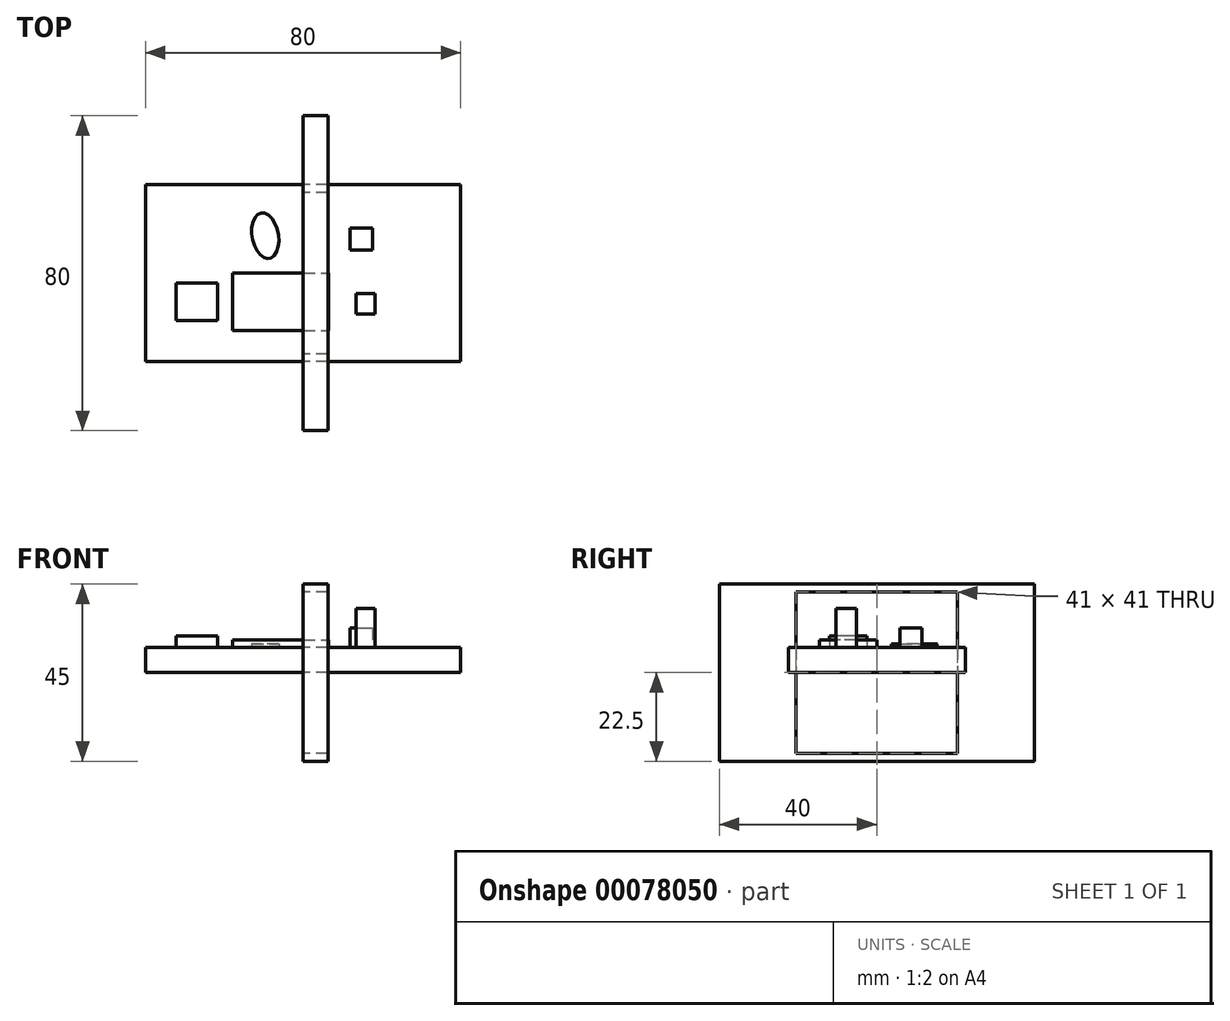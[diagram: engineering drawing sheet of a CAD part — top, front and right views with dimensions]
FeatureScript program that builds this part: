
annotation { "Feature Type Name" : "Feature", "Feature Type Description" : "" }
export const myFeature = defineFeature(function(context is Context, id is Id, definition is map)
    precondition{}
    {
        {
            var Q0;
            Q0=qCreatedBy(makeId("Right.planeOp"),FACE);
            var sketch = newSketch(context, id + "F0", { "sketchPlane" : qUnion([Q0])});
            skLineSegment(sketch, "E0.bottom", {"start": v(20.5, 20.5) * mm, "end": v(-20.5, 20.5) * mm});
            skLineSegment(sketch, "E0.top", {"start": v(20.5, -20.5) * mm, "end": v(-20.5, -20.5) * mm});
            skLineSegment(sketch, "E0.left", {"start": v(20.5, 20.5) * mm, "end": v(20.5, -20.5) * mm});
            skLineSegment(sketch, "E0.right", {"start": v(-20.5, 20.5) * mm, "end": v(-20.5, -20.5) * mm});
            skPoint(sketch, "E0.middle", {"position": v(0, 0) * mm});
            skLineSegment(sketch, "E1.bottom", {"start": v(40, 22.5) * mm, "end": v(-40, 22.5) * mm});
            skLineSegment(sketch, "E1.top", {"start": v(40, -22.5) * mm, "end": v(-40, -22.5) * mm});
            skLineSegment(sketch, "E1.left", {"start": v(40, 22.5) * mm, "end": v(40, -22.5) * mm});
            skLineSegment(sketch, "E1.right", {"start": v(-40, 22.5) * mm, "end": v(-40, -22.5) * mm});
            skSolve(sketch);
        }
        {
            var Q0;
            Q0 = qSketchRegion(id + "F0", true);
            extrude(context, id + "F1", {"entities" : qUnion([Q0]), "depth" : 6.35 * mm});
        }
        {
            var Q0;
            Q0=qCreatedBy(makeId("Top.planeOp"),FACE);
            var sketch = newSketch(context, id + "F2", { "sketchPlane" : qUnion([Q0])});
            skLineSegment(sketch, "E2.bottom", {"start": v(40, -22.5) * mm, "end": v(-40, -22.5) * mm});
            skLineSegment(sketch, "E2.top", {"start": v(40, 22.5) * mm, "end": v(-40, 22.5) * mm});
            skLineSegment(sketch, "E2.left", {"start": v(40, -22.5) * mm, "end": v(40, 22.5) * mm});
            skLineSegment(sketch, "E2.right", {"start": v(-40, -22.5) * mm, "end": v(-40, 22.5) * mm});
            skPoint(sketch, "E2.middle", {"position": v(0, 0) * mm});
            skSolve(sketch);
        }
        {
            var Q0;
            Q0 = qSketchRegion(id + "F2", true);
            extrude(context, id + "F3", {"entities" : qUnion([Q0]), "depth" : 6.35 * mm});
        }
        {
            var Q0;
            Q0=makeQuery(id+"F3.opExtrude","CAP_FACE",FACE,{"disambiguationData":[OSD([sQuery(id+"F2.wireOp",EDGE,"E2.bottom"),sQuery(id+"F2.wireOp",EDGE,"E2.top"),sQuery(id+"F2.wireOp",EDGE,"E2.left"),sQuery(id+"F2.wireOp",EDGE,"E2.right")])],"isStart":false});
            var sketch = newSketch(context, id + "F4", { "sketchPlane" : qUnion([Q0])});
            skLineSegment(sketch, "E3.bottom", {"start": v(-17.96, 0) * mm, "end": v(6.53, 0) * mm});
            skLineSegment(sketch, "E3.top", {"start": v(-17.96, -14.53) * mm, "end": v(6.53, -14.53) * mm});
            skLineSegment(sketch, "E3.left", {"start": v(-17.96, 0) * mm, "end": v(-17.96, -14.53) * mm});
            skLineSegment(sketch, "E3.right", {"start": v(6.53, 0) * mm, "end": v(6.53, -14.53) * mm});
            skLineSegment(sketch, "E4.bottom", {"start": v(-32.15, -4.1) * mm, "end": v(-21.1, -4.1) * mm});
            skLineSegment(sketch, "E4.top", {"start": v(-32.15, -10.91) * mm, "end": v(-21.1, -10.91) * mm});
            skLineSegment(sketch, "E4.left", {"start": v(-32.15, -4.1) * mm, "end": v(-32.15, -10.91) * mm});
            skLineSegment(sketch, "E4.right", {"start": v(-21.1, -4.1) * mm, "end": v(-21.1, -10.91) * mm});
            skEllipse(sketch, "E5", {"center": v(-9.88, 9.8) * mm, "majorRadius": 7.94 * mm, "minorRadius": 3.45 * mm, "majorAxis": v(-0.26, 0.97)});
            skLineSegment(sketch, "E6.bottom", {"start": v(9.26, 5.38) * mm, "end": v(14.05, 5.38) * mm});
            skLineSegment(sketch, "E6.top", {"start": v(9.26, 12.07) * mm, "end": v(14.05, 12.07) * mm});
            skLineSegment(sketch, "E6.left", {"start": v(9.26, 5.38) * mm, "end": v(9.26, 12.07) * mm});
            skLineSegment(sketch, "E6.right", {"start": v(14.05, 5.38) * mm, "end": v(14.05, 12.07) * mm});
            skLineSegment(sketch, "E7.bottom", {"start": v(12.72, -7.04) * mm, "end": v(16.48, -7.04) * mm});
            skLineSegment(sketch, "E7.top", {"start": v(12.72, -11.05) * mm, "end": v(16.48, -11.05) * mm});
            skLineSegment(sketch, "E7.left", {"start": v(12.72, -7.04) * mm, "end": v(12.72, -11.05) * mm});
            skLineSegment(sketch, "E7.right", {"start": v(16.48, -7.04) * mm, "end": v(16.48, -11.05) * mm});
            skSolve(sketch);
        }
        {
            var Q0;
            Q0=makeQuery(id+"F4.imprint","IMPRINT",FACE,{"disambiguationData":[TD([[makeQuery(id+"F4.imprint","IMPRINT",EDGE,{"derivedFrom":sQuery(id+"F4.wireOp",EDGE,"E3.bottom")}),-1.0]])]});
            extrude(context, id + "F5", {"entities" : qUnion([Q0]), "operationType" : NewBodyOperationType.ADD, "depth" : 2 * mm});
        }
        {
            var Q0;
            Q0=makeQuery(id+"F3.opExtrude","CAP_FACE",FACE,{"disambiguationData":[OSD([sQuery(id+"F2.wireOp",EDGE,"E2.bottom"),sQuery(id+"F2.wireOp",EDGE,"E2.top"),sQuery(id+"F2.wireOp",EDGE,"E2.left"),sQuery(id+"F2.wireOp",EDGE,"E2.right")])],"isStart":false});
            var sketch = newSketch(context, id + "F6", { "sketchPlane" : qUnion([Q0])});
            skLineSegment(sketch, "E8.bottom", {"start": v(-32.32, -2.55) * mm, "end": v(-21.68, -2.55) * mm});
            skLineSegment(sketch, "E8.top", {"start": v(-32.32, -12.07) * mm, "end": v(-21.68, -12.07) * mm});
            skLineSegment(sketch, "E8.left", {"start": v(-32.32, -2.55) * mm, "end": v(-32.32, -12.07) * mm});
            skLineSegment(sketch, "E8.right", {"start": v(-21.68, -2.55) * mm, "end": v(-21.68, -12.07) * mm});
            skSolve(sketch);
        }
        {
            var Q0;
            Q0 = qSketchRegion(id + "F6", true);
            extrude(context, id + "F7", {"entities" : qUnion([Q0]), "operationType" : NewBodyOperationType.ADD, "depth" : 3 * mm});
        }
        {
            var Q0;
            Q0=makeQuery(id+"F3.opExtrude","CAP_FACE",FACE,{"disambiguationData":[OSD([sQuery(id+"F2.wireOp",EDGE,"E2.bottom"),sQuery(id+"F2.wireOp",EDGE,"E2.top"),sQuery(id+"F2.wireOp",EDGE,"E2.left"),sQuery(id+"F2.wireOp",EDGE,"E2.right")])],"isStart":false});
            var sketch = newSketch(context, id + "F8", { "sketchPlane" : qUnion([Q0])});
            skEllipse(sketch, "E9", {"center": v(-9.62, 9.53) * mm, "majorRadius": 5.87 * mm, "minorRadius": 3.36 * mm, "majorAxis": v(-0.18, 0.98)});
            skSolve(sketch);
        }
        {
            var Q0;
            Q0 = qSketchRegion(id + "F8", true);
            extrude(context, id + "F9", {"entities" : qUnion([Q0]), "operationType" : NewBodyOperationType.ADD, "depth" : 1 * mm});
        }
        {
            var Q0;
            Q0=makeQuery(id+"F3.opExtrude","CAP_FACE",FACE,{"disambiguationData":[OSD([sQuery(id+"F2.wireOp",EDGE,"E2.bottom"),sQuery(id+"F2.wireOp",EDGE,"E2.top"),sQuery(id+"F2.wireOp",EDGE,"E2.left"),sQuery(id+"F2.wireOp",EDGE,"E2.right")])],"isStart":false});
            var sketch = newSketch(context, id + "F10", { "sketchPlane" : qUnion([Q0])});
            skLineSegment(sketch, "E10.bottom", {"start": v(13.41, -5.2) * mm, "end": v(18.28, -5.2) * mm});
            skLineSegment(sketch, "E10.top", {"start": v(13.41, -10.43) * mm, "end": v(18.28, -10.43) * mm});
            skLineSegment(sketch, "E10.left", {"start": v(13.41, -5.2) * mm, "end": v(13.41, -10.43) * mm});
            skLineSegment(sketch, "E10.right", {"start": v(18.28, -5.2) * mm, "end": v(18.28, -10.43) * mm});
            skSolve(sketch);
        }
        {
            var Q0;
            Q0 = qSketchRegion(id + "F10", true);
            extrude(context, id + "F11", {"entities" : qUnion([Q0]), "operationType" : NewBodyOperationType.ADD, "depth" : 10 * mm});
        }
        {
            var Q0;
            Q0=makeQuery(id+"F3.opExtrude","CAP_FACE",FACE,{"disambiguationData":[OSD([sQuery(id+"F2.wireOp",EDGE,"E2.bottom"),sQuery(id+"F2.wireOp",EDGE,"E2.top"),sQuery(id+"F2.wireOp",EDGE,"E2.left"),sQuery(id+"F2.wireOp",EDGE,"E2.right")])],"isStart":false});
            var sketch = newSketch(context, id + "F12", { "sketchPlane" : qUnion([Q0])});
            skLineSegment(sketch, "E11.bottom", {"start": v(11.93, 11.46) * mm, "end": v(17.7, 11.46) * mm});
            skLineSegment(sketch, "E11.top", {"start": v(11.93, 5.93) * mm, "end": v(17.7, 5.93) * mm});
            skLineSegment(sketch, "E11.left", {"start": v(11.93, 11.46) * mm, "end": v(11.93, 5.93) * mm});
            skLineSegment(sketch, "E11.right", {"start": v(17.7, 11.46) * mm, "end": v(17.7, 5.93) * mm});
            skSolve(sketch);
        }
        {
            var Q0;
            Q0=makeQuery(id+"F12.imprint","IMPRINT",FACE,{"disambiguationData":[TD([[makeQuery(id+"F12.imprint","IMPRINT",EDGE,{"derivedFrom":sQuery(id+"F12.wireOp",EDGE,"E11.bottom")}),-1.0]])]});
            extrude(context, id + "F13", {"entities" : qUnion([Q0]), "operationType" : NewBodyOperationType.ADD, "depth" : 5 * mm});
        }
    });
